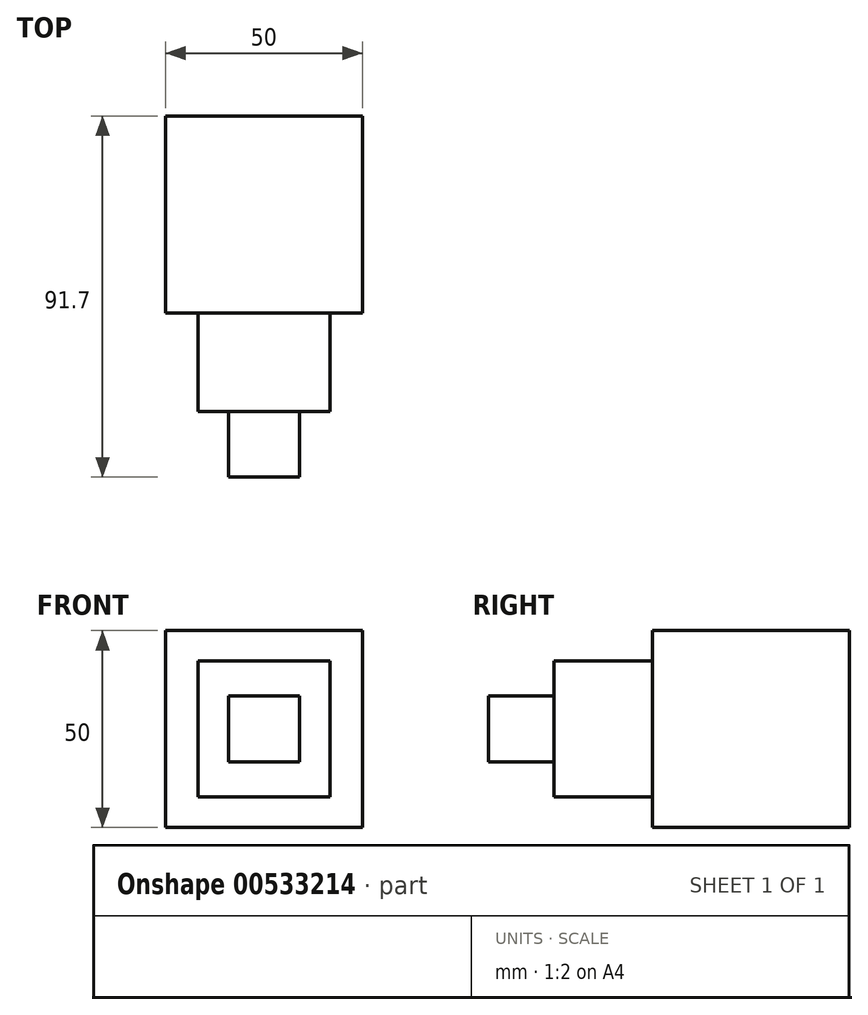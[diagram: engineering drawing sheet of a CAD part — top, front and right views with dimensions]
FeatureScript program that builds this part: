
annotation { "Feature Type Name" : "Feature", "Feature Type Description" : "" }
export const myFeature = defineFeature(function(context is Context, id is Id, definition is map)
    precondition{}
    {
        {
            var Q0;
            Q0=qCreatedBy(makeId("Front.planeOp"),FACE);
            var sketch = newSketch(context, id + "F0", { "sketchPlane" : qUnion([Q0])});
            skLineSegment(sketch, "E0.bottom", {"start": v(-25, 25) * mm, "end": v(25, 25) * mm});
            skLineSegment(sketch, "E0.top", {"start": v(-25, -25) * mm, "end": v(25, -25) * mm});
            skLineSegment(sketch, "E0.left", {"start": v(-25, 25) * mm, "end": v(-25, -25) * mm});
            skLineSegment(sketch, "E0.right", {"start": v(25, 25) * mm, "end": v(25, -25) * mm});
            skSolve(sketch);
        }
        {
            var Q0;
            Q0 = qSketchRegion(id + "F0", true);
            extrude(context, id + "F1", {"entities" : qUnion([Q0]), "depth" : 50 * mm, "offsetDistance" : 25 * mm});
        }
        {
            var Q0;
            Q0=makeQuery(id+"F1.opExtrude","CAP_FACE",FACE,{"disambiguationData":[OSD([sQuery(id+"F0.wireOp",EDGE,"E0.bottom"),sQuery(id+"F0.wireOp",EDGE,"E0.top"),sQuery(id+"F0.wireOp",EDGE,"E0.left"),sQuery(id+"F0.wireOp",EDGE,"E0.right")])],"isStart":false});
            var sketch = newSketch(context, id + "F2", { "sketchPlane" : qUnion([Q0])});
            skLineSegment(sketch, "E1.bottom", {"start": v(16.74, 17.23) * mm, "end": v(-16.74, 17.23) * mm});
            skLineSegment(sketch, "E1.top", {"start": v(16.74, -17.23) * mm, "end": v(-16.74, -17.23) * mm});
            skLineSegment(sketch, "E1.left", {"start": v(16.74, 17.23) * mm, "end": v(16.74, -17.23) * mm});
            skLineSegment(sketch, "E1.right", {"start": v(-16.74, 17.23) * mm, "end": v(-16.74, -17.23) * mm});
            skPoint(sketch, "E1.middle", {"position": v(0, 0) * mm});
            skSolve(sketch);
        }
        {
            var Q0;
            Q0=makeQuery(id+"F2.imprint","IMPRINT",FACE,{"disambiguationData":[TD([[makeQuery(id+"F2.imprint","IMPRINT",EDGE,{"derivedFrom":sQuery(id+"F2.wireOp",EDGE,"E1.bottom")}),1.0]])]});
            extrude(context, id + "F3", {"entities" : qUnion([Q0]), "operationType" : NewBodyOperationType.ADD, "depth" : 25 * mm, "offsetDistance" : 25 * mm});
        }
        {
            var Q0;
            Q0=makeQuery(id+"F3.opExtrude","CAP_FACE",FACE,{"disambiguationData":[OSD([sQuery(id+"F2.wireOp",EDGE,"E1.bottom"),sQuery(id+"F2.wireOp",EDGE,"E1.top"),sQuery(id+"F2.wireOp",EDGE,"E1.left"),sQuery(id+"F2.wireOp",EDGE,"E1.right")])],"isStart":false});
            var sketch = newSketch(context, id + "F4", { "sketchPlane" : qUnion([Q0])});
            skLineSegment(sketch, "E2.bottom", {"start": v(9.02, 8.42) * mm, "end": v(-9.02, 8.42) * mm});
            skLineSegment(sketch, "E2.top", {"start": v(9.02, -8.42) * mm, "end": v(-9.02, -8.42) * mm});
            skLineSegment(sketch, "E2.left", {"start": v(9.02, 8.42) * mm, "end": v(9.02, -8.42) * mm});
            skLineSegment(sketch, "E2.right", {"start": v(-9.02, 8.42) * mm, "end": v(-9.02, -8.42) * mm});
            skPoint(sketch, "E2.middle", {"position": v(0, 0) * mm});
            skSolve(sketch);
        }
        {
            var Q0;
            Q0 = qSketchRegion(id + "F4", true);
            var Q1;
            Q1=makeQuery(id+"F4.imprint","IMPRINT",FACE,{"disambiguationData":[TD([[makeQuery(id+"F4.imprint","IMPRINT",EDGE,{"derivedFrom":sQuery(id+"F4.wireOp",EDGE,"E2.bottom")}),1.0]])]});
            extrude(context, id + "F5", {"entities" : qUnion([Q0, Q1]), "operationType" : NewBodyOperationType.ADD, "endBound" : BoundingType.SYMMETRIC, "depth" : 33.4 * mm, "offsetDistance" : 25 * mm});
        }
    });
